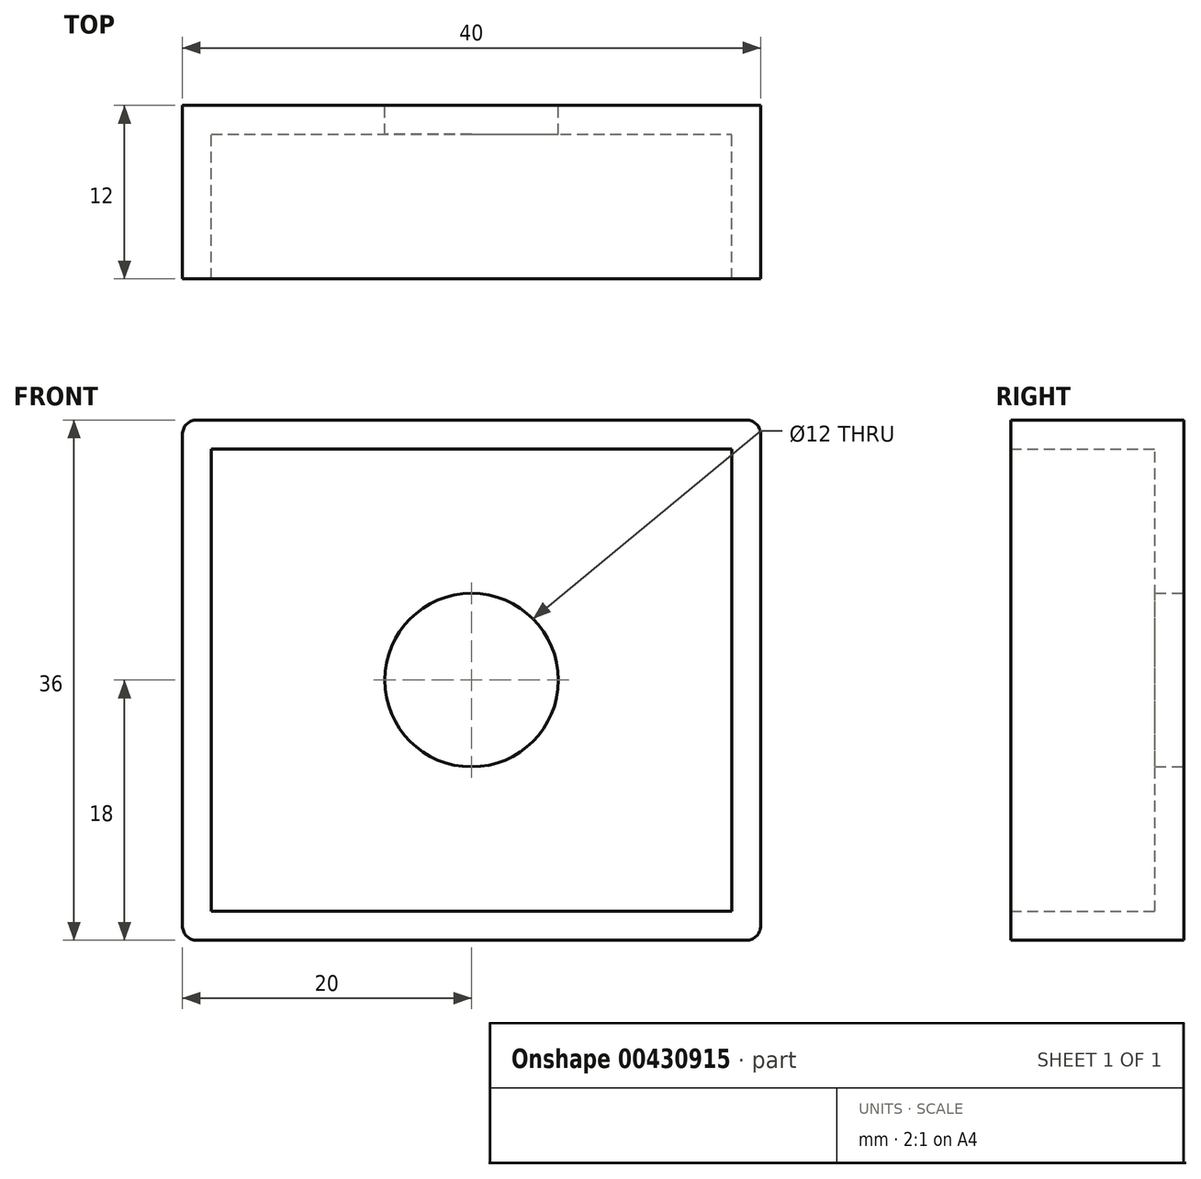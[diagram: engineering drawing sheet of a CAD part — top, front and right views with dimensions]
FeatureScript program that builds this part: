
annotation { "Feature Type Name" : "Feature", "Feature Type Description" : "" }
export const myFeature = defineFeature(function(context is Context, id is Id, definition is map)
    precondition{}
    {
        {
            var Q0;
            Q0=qCreatedBy(makeId("Front.planeOp"),FACE);
            var sketch = newSketch(context, id + "F0", { "sketchPlane" : qUnion([Q0])});
            skLineSegment(sketch, "E0.bottom", {"start": v(0, 0) * mm, "end": v(40, 0) * mm});
            skLineSegment(sketch, "E0.top", {"start": v(0, 36) * mm, "end": v(40, 36) * mm});
            skLineSegment(sketch, "E0.left", {"start": v(0, 0) * mm, "end": v(0, 36) * mm});
            skLineSegment(sketch, "E0.right", {"start": v(40, 0) * mm, "end": v(40, 36) * mm});
            skSolve(sketch);
        }
        {
            var Q0;
            Q0=makeQuery(id+"F0.imprint","IMPRINT",FACE,{"disambiguationData":[TD([[makeQuery(id+"F0.imprint","IMPRINT",EDGE,{"derivedFrom":sQuery(id+"F0.wireOp",EDGE,"E0.bottom")}),1.0]])]});
            extrude(context, id + "F1", {"entities" : qUnion([Q0]), "depth" : 12 * mm});
        }
        {
            var Q0;
            Q0=makeQuery(id+"F1.opExtrude","CAP_FACE",FACE,{"disambiguationData":[OSD([sQuery(id+"F0.wireOp",EDGE,"E0.bottom"),sQuery(id+"F0.wireOp",EDGE,"E0.top"),sQuery(id+"F0.wireOp",EDGE,"E0.left"),sQuery(id+"F0.wireOp",EDGE,"E0.right"),sQuery(id+"F0.wireOp",EDGE,"CaBhea8C-fdAB-pH6J-BXqY-UUMMSboF16yI")])],"isStart":false});
            shell(context, id + "F2", {"entities" : qUnion([Q0]), "thickness" : 2 * mm});
        }
        {
            var Q0;
            Q0=makeQuery(id+"F1.opExtrude","CAP_FACE",FACE,{"disambiguationData":[OSD([sQuery(id+"F0.wireOp",EDGE,"E0.bottom"),sQuery(id+"F0.wireOp",EDGE,"E0.top"),sQuery(id+"F0.wireOp",EDGE,"E0.left"),sQuery(id+"F0.wireOp",EDGE,"E0.right")])],"isStart":true});
            var sketch = newSketch(context, id + "F3", { "sketchPlane" : qUnion([Q0])});
            skCircle(sketch, "E1", {"center": v(-20, 18) * mm, "radius": 6 * mm});
            skPoint(sketch, "E1.centerSnap0", {"position": v(-20, 0) * mm});
            skPoint(sketch, "E1.centerSnap1", {"position": v(-40, 18) * mm});
            skSolve(sketch);
        }
        {
            var Q0;
            Q0=makeQuery(id+"F3.imprint","IMPRINT",FACE,{"disambiguationData":[TD([[makeQuery(id+"F3.imprint","IMPRINT",EDGE,{"derivedFrom":sQuery(id+"F3.wireOp",EDGE,"E1")}),1.0]])]});
            var Q1;
            Q1=sQuery(id+"F3.wireOp",EDGE,"E1");
            extrude(context, id + "F4", {"entities" : qUnion([Q0]), "operationType" : NewBodyOperationType.REMOVE, "surfaceEntities" : qUnion([Q1]), "oppositeDirection" : true, "depth" : 25 * mm});
        }
        {
            var Q0;
            Q0=makeQuery(id+"F1.opExtrude","SWEPT_EDGE",EDGE,{"disambiguationData":[OSD([sQuery(id+"F0.wireOp",EDGE,"E0.bottom"),sQuery(id+"F0.wireOp",EDGE,"E0.right")])]});
            var Q1;
            Q1=makeQuery(id+"F1.opExtrude","SWEPT_EDGE",EDGE,{"disambiguationData":[OSD([sQuery(id+"F0.wireOp",EDGE,"E0.top"),sQuery(id+"F0.wireOp",EDGE,"E0.right")])]});
            var Q2;
            Q2=makeQuery(id+"F1.opExtrude","SWEPT_EDGE",EDGE,{"disambiguationData":[OSD([sQuery(id+"F0.wireOp",EDGE,"E0.bottom"),sQuery(id+"F0.wireOp",EDGE,"E0.left")])]});
            var Q3;
            Q3=makeQuery(id+"F1.opExtrude","SWEPT_EDGE",EDGE,{"disambiguationData":[OSD([sQuery(id+"F0.wireOp",EDGE,"E0.top"),sQuery(id+"F0.wireOp",EDGE,"E0.left")])]});
            fillet(context, id + "F5", {"entities" : qUnion([Q0, Q1, Q2, Q3]), "radius" : 1 * mm, "tangentPropagation" : true, "allowEdgeOverflow" : false});
        }
    });
